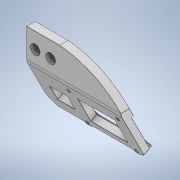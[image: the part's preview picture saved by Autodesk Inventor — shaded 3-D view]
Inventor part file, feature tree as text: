
AUTODESK INVENTOR PART (.ipt)
format: ipt  version: 2021 (Build 250183000, 183)  size: 474,112 bytes
history: native  units: mm
features: extrude x6, sketch x5, projected_geometry x4, revolve x1, fillet x1
ambient origin geometry x8: Origin, YZ Plane, XZ Plane, XY Plane, X Axis, Y Axis, Z Axis, Center Point
bodies: Solid1 (feature_tree)
feature tree (17):
  sketch  "Sketch1"  dims[d0=4.3mm d1=4.3mm d2=11.6mm d3=8.05mm d4=11.6mm d5=8.5mm d6=8.5mm d7=86.23mm d8=8.0mm d9=0.0mm]
  extrude  "Extrusion1"  Depth=8.0mm TaperAngle=0.0deg
  extrude  "Extrusion2"  Depth=4.0mm
  revolve  "Revolution1"  [1 undecoded]
  extrude  "Extrusion3"  Depth=6.6mm
  sketch  "Sketch5"  dims[d37=6.6mm d38=6.6mm]
  extrude  "Extrusion4"  Depth=0.2mm
  extrude  "Extrusion5"  Depth=0.2mm
  extrude  "Extrusion6"  Depth=0.2mm
  fillet  "Fillet1"  Radius=3.2mm
  sketch  "Sketch2"  dims[d10=4.0mm d11=0.0mm d12=4.712389mm]
  projected_geometry  "Projected Loop1"
  sketch  "Sketch3"  dims[d13=49.0mm d14=0.0mm d36=3.2mm]
  projected_geometry  "Projected Loop2"
  projected_geometry  "Projected Loop4"
  sketch  "Sketch6"  dims[d39=3.2mm d40=48.0mm d41=3.2mm d42=41.0mm d43=3.2mm d44=33.8mm d45=26.8mm d46=5.5mm d47=5.5mm d48=16.0mm d49=16.0mm d50=12.182mm d51=11.523mm d52=8.0mm d53=8.0mm d54=8.0mm d55=8.0mm d56=0.0mm d57=0.0mm d58=2.0mm d59=0.0mm d60=30.23mm d61=0.0mm d62=0.0mm d63=0.2mm d64=0.2mm d65=0.2mm d66=0.872665mm d67=0.872665mm]
  projected_geometry  "Projected Loop5"
note: 1 required parameter value undecoded (feature->parameter linkage not recoverable at this tier; creation-order binding heuristic only, values carry confidence <= 0.55)
